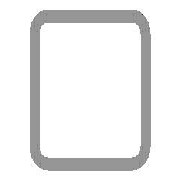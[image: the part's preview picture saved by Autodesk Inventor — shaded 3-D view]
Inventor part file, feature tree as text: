
AUTODESK INVENTOR PART (.ipt)
format: ipt  version: 2022 (Build 260153000, 153)  size: 176,128 bytes
history: native  units: mm (DEFAULTED — no unit token found)
features: other x5, sketch x2, sweep x1, plane x1
ambient origin geometry x8: Origin, YZ Plane, XZ Plane, XY Plane, X Axis, Y Axis, Z Axis, Center Point
bodies: Solid1 (feature_tree), Body (feature_tree)
feature tree (9):
  parser-record x1  (decoder bookkeeping rows leaked as tree rows — omitted from the tree; the rows remain in map.json)
  other  "Driven Length"
  other  "Start Plane"
  other  "End Plane"
  sweep  "Sweep Path"
  other  "Orientation Work Plane"
  sketch  "Sketch3"  dims[d7=8.0mm d9=40.0mm]
  plane  "Work Plane3"
  sketch  "Sketch4"  dims[d11=40.0mm d12=4.0mm d13=-0.0mm d14=3515.406592mm d15=20.0mm d16=20.0mm d17=90.0deg d18=3515.406592mm d19=0.0mm d20=0.0mm]
